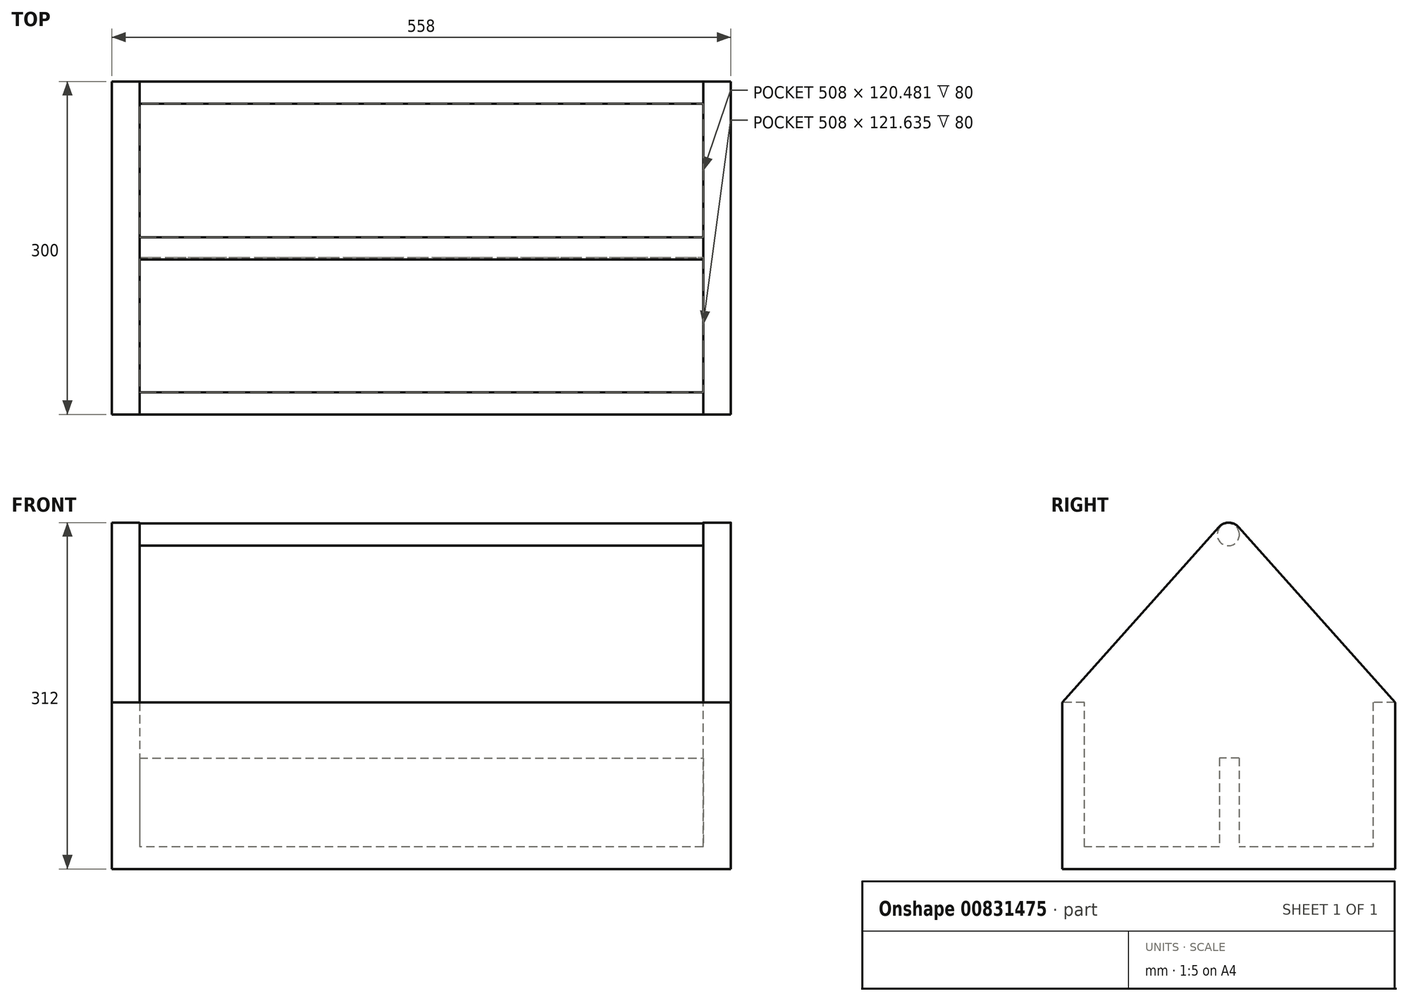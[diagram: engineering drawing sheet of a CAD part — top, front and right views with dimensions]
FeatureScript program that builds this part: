
annotation { "Feature Type Name" : "Feature", "Feature Type Description" : "" }
export const myFeature = defineFeature(function(context is Context, id is Id, definition is map)
    precondition{}
    {
        {
            var Q0;
            Q0=qCreatedBy(makeId("Right.planeOp"),FACE);
            var sketch = newSketch(context, id + "F0", { "sketchPlane" : qUnion([Q0])});
            skLineSegment(sketch, "E0", {"start": v(-97.45, -26.33) * mm, "end": v(202.55, -26.33) * mm});
            skLineSegment(sketch, "E1", {"start": v(202.55, 123.67) * mm, "end": v(202.55, -26.33) * mm});
            skLineSegment(sketch, "E2", {"start": v(-97.45, -26.33) * mm, "end": v(-97.45, 123.67) * mm});
            skArc(sketch, "E3", {"start": v(61.5, 281.66) * mm, "mid": v(52.55, 285.67) * mm, "end": v(43.6, 281.66) * mm});
            skPoint(sketch, "E3.centerSnap0", {"position": v(52.55, -26.33) * mm});
            skLineSegment(sketch, "E4", {"start": v(-97.45, 123.67) * mm, "end": v(43.6, 281.66) * mm});
            skLineSegment(sketch, "E5", {"start": v(202.55, 123.67) * mm, "end": v(61.5, 281.66) * mm});
            skSolve(sketch);
        }
        {
            var Q0;
            Q0 = qSketchRegion(id + "F0", true);
            extrude(context, id + "F1", {"entities" : qUnion([Q0]), "depth" : 25 * mm, "offsetDistance" : 25 * mm});
        }
        {
            var Q0;
            Q0=makeQuery(id+"F1.opExtrude","CAP_FACE",FACE,{"disambiguationData":[OSD([sQuery(id+"F0.wireOp",EDGE,"E0"),sQuery(id+"F0.wireOp",EDGE,"E1"),sQuery(id+"F0.wireOp",EDGE,"E2"),sQuery(id+"F0.wireOp",EDGE,"E3"),sQuery(id+"F0.wireOp",EDGE,"E4"),sQuery(id+"F0.wireOp",EDGE,"E5")])],"isStart":true});
            var sketch = newSketch(context, id + "F2", { "sketchPlane" : qUnion([Q0])});
            skLineSegment(sketch, "E6", {"start": v(-202.55, 123.67) * mm, "end": v(-182.55, 123.67) * mm});
            skLineSegment(sketch, "E7", {"start": v(-182.55, 123.67) * mm, "end": v(-182.55, -6.33) * mm});
            skLineSegment(sketch, "E8", {"start": v(-182.55, -6.33) * mm, "end": v(77.45, -6.33) * mm});
            skLineSegment(sketch, "E9", {"start": v(97.45, 123.67) * mm, "end": v(97.45, 123.67) * mm});
            skLineSegment(sketch, "E10", {"start": v(77.45, -6.33) * mm, "end": v(77.45, 123.67) * mm});
            skLineSegment(sketch, "E11", {"start": v(77.45, 123.67) * mm, "end": v(97.45, 123.67) * mm});
            skSolve(sketch);
        }
        {
            var Q0;
            Q0 = qSketchRegion(id + "F2", true);
            var Q1;
            Q1=makeQuery(id+"F2.imprint","IMPRINT",FACE,{"disambiguationData":[TD([[makeQuery(id+"F2.imprint","IMPRINT",EDGE,{"derivedFrom":sQuery(id+"F2.wireOp",EDGE,"E6")}),-1.0]])]});
            extrude(context, id + "F3", {"entities" : qUnion([Q0, Q1]), "operationType" : NewBodyOperationType.ADD, "depth" : 508 * mm, "offsetDistance" : 25 * mm});
        }
        {
            var Q0;
            Q0=makeQuery(id+"F3.opExtrude","CAP_FACE",FACE,{"disambiguationData":[OSD([sQuery(id+"F0.wireOp",EDGE,"E0"),sQuery(id+"F0.wireOp",EDGE,"E1"),sQuery(id+"F0.wireOp",EDGE,"E2"),sQuery(id+"F2.wireOp",EDGE,"E6"),sQuery(id+"F2.wireOp",EDGE,"E7"),sQuery(id+"F2.wireOp",EDGE,"E8"),sQuery(id+"F2.wireOp",EDGE,"NgHp8GeH-2828-YXRl-GsCZ-DGXQ4YvgHPgH"),sQuery(id+"F2.wireOp",EDGE,"E9")])],"isStart":false});
            var sketch = newSketch(context, id + "F4", { "sketchPlane" : qUnion([Q0])});
            skArc(sketch, "E12", {"start": v(-43.6, 281.66) * mm, "mid": v(-52.55, 285.67) * mm, "end": v(-61.5, 281.66) * mm});
            skLineSegment(sketch, "E13", {"start": v(-202.55, 123.67) * mm, "end": v(-61.5, 281.66) * mm});
            skLineSegment(sketch, "E14", {"start": v(97.45, 123.67) * mm, "end": v(-43.6, 281.66) * mm});
            skLineSegment(sketch, "E15", {"start": v(97.45, 123.67) * mm, "end": v(97.45, -26.33) * mm});
            skLineSegment(sketch, "E16", {"start": v(97.45, -26.33) * mm, "end": v(-202.55, -26.33) * mm});
            skLineSegment(sketch, "E17", {"start": v(-202.55, -26.33) * mm, "end": v(-202.55, 123.67) * mm});
            skSolve(sketch);
        }
        {
            var Q0;
            Q0 = qSketchRegion(id + "F4", true);
            extrude(context, id + "F5", {"entities" : qUnion([Q0]), "operationType" : NewBodyOperationType.ADD, "depth" : 25 * mm, "offsetDistance" : 25 * mm});
        }
        {
            var Q0;
            Q0=makeQuery(id+"F0.imprint","IMPRINT",FACE,{"disambiguationData":[TD([[makeQuery(id+"F0.imprint","IMPRINT",EDGE,{"derivedFrom":sQuery(id+"F0.wireOp",EDGE,"E0")}),1.0]])]});
            var sketch = newSketch(context, id + "F6", { "sketchPlane" : qUnion([Q0])});
            skCircle(sketch, "E18", {"center": v(52.24, 274.9) * mm, "radius": 10 * mm});
            skSolve(sketch);
        }
        {
            var Q0;
            Q0 = qSketchRegion(id + "F6", true);
            extrude(context, id + "F7", {"entities" : qUnion([Q0]), "operationType" : NewBodyOperationType.ADD, "oppositeDirection" : true, "depth" : 508 * mm, "offsetDistance" : 25 * mm});
        }
        {
            var Q0;
            Q0=makeQuery(id+"F3.opExtrude","SWEPT_FACE",FACE,{"disambiguationData":[OSD([sQuery(id+"F2.wireOp",EDGE,"E8")])]});
            var sketch = newSketch(context, id + "F8", { "sketchPlane" : qUnion([Q0])});
            skLineSegment(sketch, "E19", {"start": v(-508, 44.18) * mm, "end": v(0, 44.18) * mm});
            skLineSegment(sketch, "E20", {"start": v(0, 44.18) * mm, "end": v(0, 62.07) * mm});
            skLineSegment(sketch, "E21", {"start": v(0, 62.07) * mm, "end": v(-508, 62.07) * mm});
            skLineSegment(sketch, "E22", {"start": v(-508, 62.07) * mm, "end": v(-508, 44.18) * mm});
            skSolve(sketch);
        }
        {
            var Q0;
            Q0=makeQuery(id+"F8.imprint","IMPRINT",FACE,{"disambiguationData":[TD([[makeQuery(id+"F8.imprint","IMPRINT",EDGE,{"derivedFrom":sQuery(id+"F8.wireOp",EDGE,"E19")}),1.0]])]});
            extrude(context, id + "F9", {"entities" : qUnion([Q0]), "operationType" : NewBodyOperationType.ADD, "depth" : 80 * mm, "offsetDistance" : 25 * mm});
        }
    });
